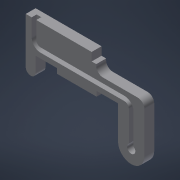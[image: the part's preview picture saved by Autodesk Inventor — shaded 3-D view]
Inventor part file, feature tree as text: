
AUTODESK INVENTOR PART (.ipt)
format: ipt  version: 2021 (Build 250183000, 183)  size: 164,864 bytes
history: native  units: mm
features: other x5, extrude x4, reference x4, sketch x3, fillet x1, projected_geometry x1
ambient origin geometry x8: Origin, YZ Plane, XZ Plane, XY Plane, X Axis, Y Axis, Z Axis, Center Point
bodies: Body1 (feature_tree)
feature tree (18):
  other  "Твердое тело1"
  extrude  "Выдавливание1"  Depth=2.5mm
  extrude  "Выдавливание2"  Depth=3.0mm TaperAngle=0.0deg
  fillet  "Сопряжение1"  Radius=1.0mm
  extrude  "Выдавливание3"  Depth=2.0mm
  sketch  "Эскиз4"
  other  "РабПлоскость1"
  extrude  "Выдавливание4"  Depth=1.5mm
  sketch  "Эскиз1"
  sketch  "Эскиз2"
  projected_geometry  "Спроецированная петля1"
  reference  "Ссылка2"
  reference  "Ссылка3"
  reference  "Ссылка4"
  reference  "Ссылка5"
  other  "<userpath>\Documents\GitHub\Tesla_coil_V1\3dModels\TeslaCoil.iam"
  other  "TeslaCoil.iam"
  other  "PrimaryTab:1"
